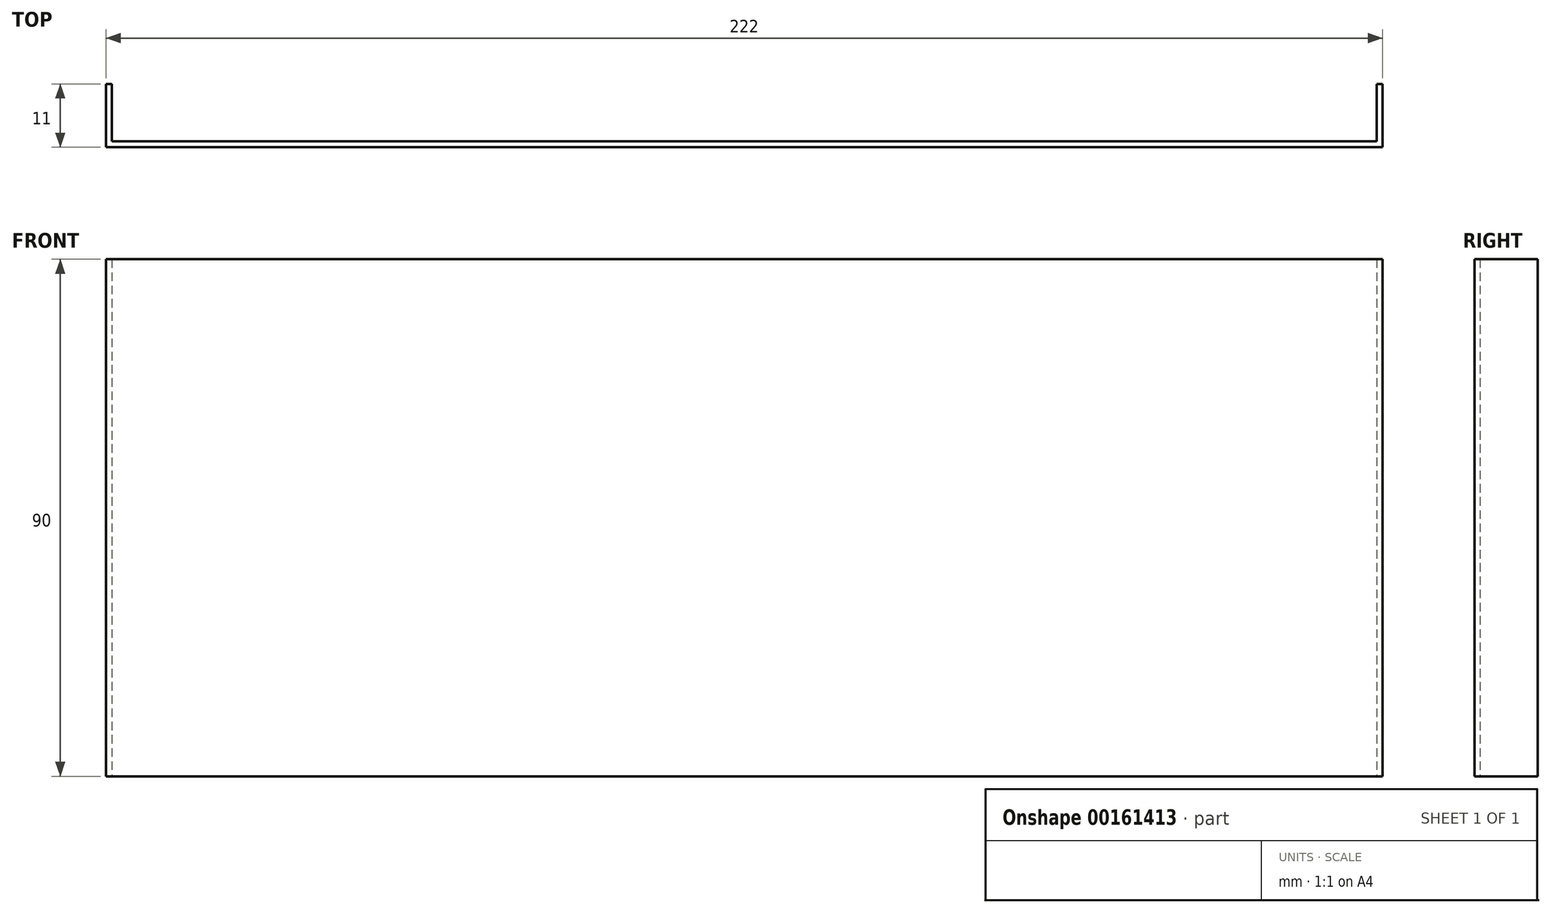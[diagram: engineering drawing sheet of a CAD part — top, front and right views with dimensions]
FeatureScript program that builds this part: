
annotation { "Feature Type Name" : "Feature", "Feature Type Description" : "" }
export const myFeature = defineFeature(function(context is Context, id is Id, definition is map)
    precondition{}
    {
        {
            var Q0;
            Q0=qCreatedBy(makeId("Front.planeOp"),FACE);
            var sketch = newSketch(context, id + "F0", { "sketchPlane" : qUnion([Q0])});
            skLineSegment(sketch, "E0.bottom", {"start": v(111, 40.92) * mm, "end": v(60.5, 40.92) * mm});
            skLineSegment(sketch, "E0.top", {"start": v(111, -49.08) * mm, "end": v(-111, -49.08) * mm});
            skLineSegment(sketch, "E0.left", {"start": v(111, 40.92) * mm, "end": v(111, -49.08) * mm});
            skLineSegment(sketch, "E0.right", {"start": v(-111, 40.92) * mm, "end": v(-111, -49.08) * mm});
            skPoint(sketch, "E0.middle", {"position": v(0, -4.08) * mm});
            skLineSegment(sketch, "E1.trimOffspring", {"start": v(0, 40.92) * mm, "end": v(-111, 40.92) * mm});
            skLineSegment(sketch, "E2", {"start": v(0, 40.92) * mm, "end": v(60.5, 40.92) * mm});
            skSolve(sketch);
        }
        {
            var Q0;
            Q0=qSketchRegion(id+"F0",true);
            extrude(context, id + "F1", {"entities" : qUnion([Q0]), "depth" : 1 * mm});
        }
        {
            var Q0;
            Q0=makeQuery(id+"F1.opExtrude","CAP_FACE",FACE,{"disambiguationData":[OSD([sQuery(id+"F0.wireOp",EDGE,"E0.bottom"),sQuery(id+"F0.wireOp",EDGE,"E0.top"),sQuery(id+"F0.wireOp",EDGE,"E0.left"),sQuery(id+"F0.wireOp",EDGE,"E0.right"),sQuery(id+"F0.wireOp",EDGE,"lcNc1bah-wNpo-JnWk-p5HF-Xycvgny5CtKj.top"),sQuery(id+"F0.wireOp",EDGE,"lcNc1bah-wNpo-JnWk-p5HF-Xycvgny5CtKj.left"),sQuery(id+"F0.wireOp",EDGE,"lcNc1bah-wNpo-JnWk-p5HF-Xycvgny5CtKj.right"),sQuery(id+"F0.wireOp",EDGE,"E1.trimOffspring")])],"isStart":true});
            var sketch = newSketch(context, id + "F2", { "sketchPlane" : qUnion([Q0])});
            skLineSegment(sketch, "E3.bottom", {"start": v(-111, 40.92) * mm, "end": v(-110, 40.92) * mm});
            skLineSegment(sketch, "E3.top", {"start": v(-111, -49.08) * mm, "end": v(-110, -49.08) * mm});
            skLineSegment(sketch, "E3.left", {"start": v(-111, 40.92) * mm, "end": v(-111, -49.08) * mm});
            skLineSegment(sketch, "E3.right", {"start": v(-110, 40.92) * mm, "end": v(-110, -49.08) * mm});
            skLineSegment(sketch, "E4.bottom", {"start": v(111, 40.92) * mm, "end": v(110, 40.92) * mm});
            skLineSegment(sketch, "E4.top", {"start": v(111, -49.08) * mm, "end": v(110, -49.08) * mm});
            skLineSegment(sketch, "E4.left", {"start": v(111, 40.92) * mm, "end": v(111, -49.08) * mm});
            skLineSegment(sketch, "E4.right", {"start": v(110, 40.92) * mm, "end": v(110, -49.08) * mm});
            skSolve(sketch);
        }
        {
            var Q0;
            Q0=qSketchRegion(id+"F2",true);
            extrude(context, id + "F3", {"entities" : qUnion([Q0]), "operationType" : NewBodyOperationType.ADD, "depth" : 10 * mm});
        }
    });
